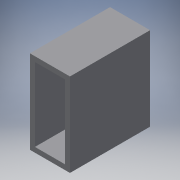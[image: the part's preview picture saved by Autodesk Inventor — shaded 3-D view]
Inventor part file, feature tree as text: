
AUTODESK INVENTOR PART (.ipt)
format: ipt  version: 2016 (Build 200138000, 138)  size: 107,520 bytes
history: native  units: in
note: dims shown in document units (in); Inventor stores cm internally (conversion verified against a paired STEP export)
features: sketch x3, extrude x2
ambient origin geometry x8: Origin, YZ Plane, XZ Plane, XY Plane, X Axis, Y Axis, Z Axis, Center Point
bodies: Solid1 (feature_tree)
feature tree (5):
  sketch  "Sketch1"  dims[d0=0.125in d1=0.125in]
  extrude  "Extrusion1"  Depth=0.125in
  extrude  "Extrusion2"  Depth=0.125in
  sketch  "Sketch2"  dims[d2=0.125in d3=0.125in]
  sketch  "Sketch3"  dims[d4=2.0in d5=1.0in d6=2.0in d7=2.0in d8=0.0in d9=1.125in d10=1.0in d11=1.0in d12=2.0in d13=0.0in]
